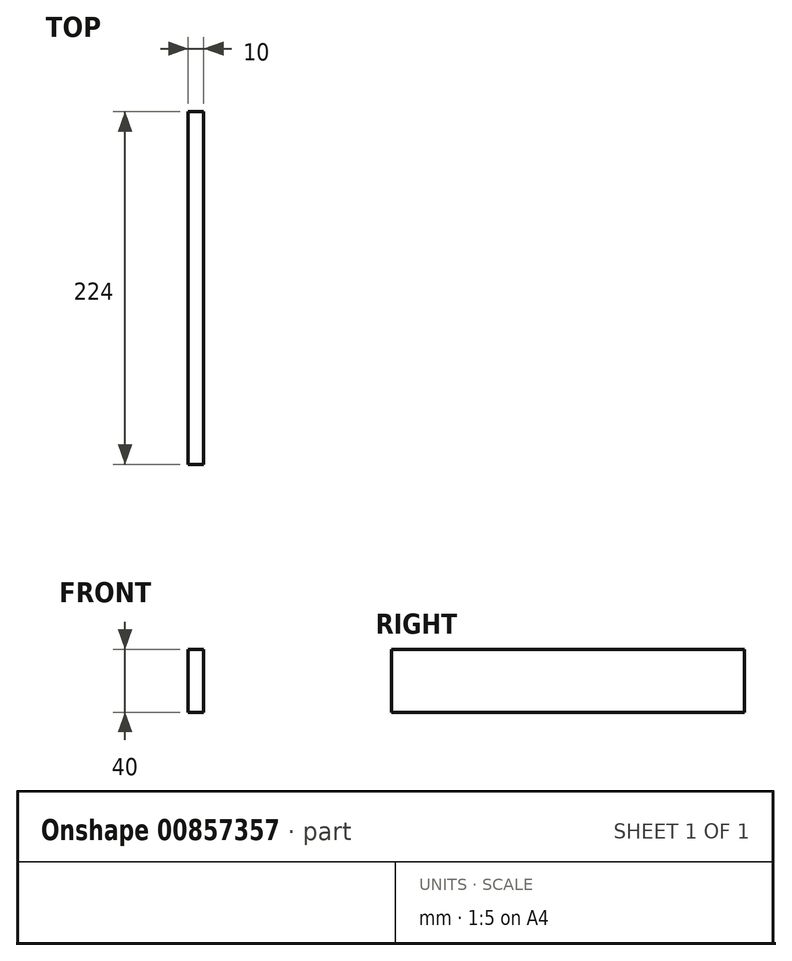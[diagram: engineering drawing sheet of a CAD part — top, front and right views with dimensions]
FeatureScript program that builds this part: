
annotation { "Feature Type Name" : "Feature", "Feature Type Description" : "" }
export const myFeature = defineFeature(function(context is Context, id is Id, definition is map)
    precondition{}
    {
        {
            var Q0;
            Q0=qCreatedBy(makeId("Front.planeOp"),FACE);
            var sketch = newSketch(context, id + "F0", { "sketchPlane" : qUnion([Q0])});
            skLineSegment(sketch, "E0.bottom", {"start": v(-14.1, 20.06) * mm, "end": v(-4.1, 20.06) * mm});
            skLineSegment(sketch, "E0.top", {"start": v(-14.1, -19.94) * mm, "end": v(-4.1, -19.94) * mm});
            skLineSegment(sketch, "E0.left", {"start": v(-14.1, 20.06) * mm, "end": v(-14.1, -19.94) * mm});
            skLineSegment(sketch, "E0.right", {"start": v(-4.1, 20.06) * mm, "end": v(-4.1, -19.94) * mm});
            skSolve(sketch);
        }
        {
            var Q0;
            Q0=makeQuery(id+"F0.imprint","IMPRINT",FACE,{"disambiguationData":[TD([[makeQuery(id+"F0.imprint","IMPRINT",EDGE,{"derivedFrom":sQuery(id+"F0.wireOp",EDGE,"E0.bottom")}),-1.0]])]});
            extrude(context, id + "F1", {"entities" : qUnion([Q0]), "depth" : 224 * mm, "offsetDistance" : 25 * mm});
        }
    });
